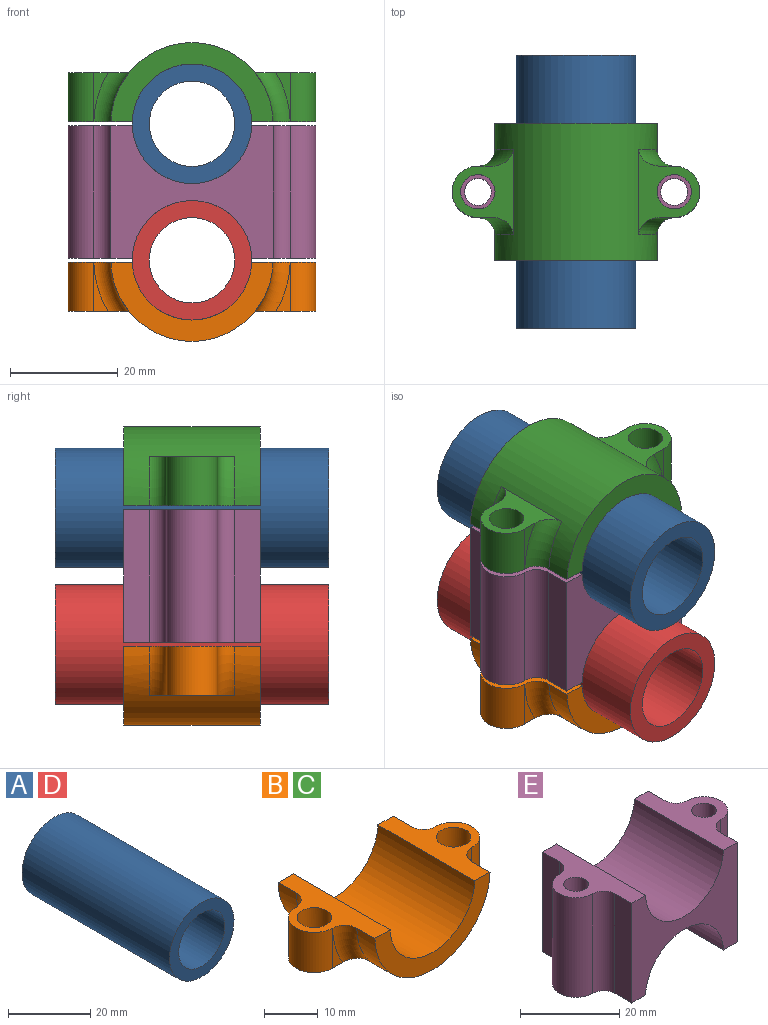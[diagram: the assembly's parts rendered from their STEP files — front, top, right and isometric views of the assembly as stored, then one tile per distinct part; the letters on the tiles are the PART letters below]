
ASSEMBLY  parts=5 mates=4
PART A: 4 faces, bbox 22.2x50.8x22.2 mm
  f0: cylinder r=7.94mm len=50.8mm, axis (0,1,0), area 2533.5mm2, adj f2,f3
  f1: cylinder r=11.11mm len=50.8mm, axis (0,1,0), area 3547mm2, adj f2,f3
  f2: plane 22.23x22.23mm, normal (0,-1,0), area 190mm2, adj f0,f1
  f3: plane 22.23x22.23mm, normal (0,1,0), area 190mm2, adj f0,f1
PART B: 20 faces, bbox 46.1x25.4x14.8 mm
  f0: cylinder r=15.09mm len=30.17mm, axis (0,1,0), area 868.6mm2, adj f1,f2,f4,f5,f6,f10,f11,f13
  f1: plane 25.43x11.96mm, normal (0,0,1), area 139.4mm2, adj f0,f3,f4,f5,f7,f8,f9,f10
  f2: plane 25.43x11.96mm, normal (0,0,1), area 139.4mm2, adj f0,f3,f4,f5,f14,f15,f16,f17
  f3: cylinder r=11.11mm len=25.4mm, axis (0,1,0), area 866.7mm2, adj f1,f2,f4,f5
  f4: plane 30.17x14.69mm, normal (0,-1,0), area 160.5mm2, adj f0,f1,f2,f3
  f5: plane 30.17x14.69mm, normal (0,1,0), area 160.5mm2, adj f0,f1,f2,f3
  f6: plane 15.9x11.34mm, normal (0,0,-1), area 71.7mm2, adj f0,f7,f8,f9,f10,f11,f12
  f7: plane 9.13x2.68mm, normal (0,-1,0), area 8.2mm2, adj f1,f6,f9,f11
  f8: plane 9.13x2.68mm, normal (0,1,0), area 8.2mm2, adj f1,f6,f9,f10
  f9: cylinder r=4.78mm len=9.55mm, axis (0,0,1), area 137mm2, adj f1,f6,f7,f8
  f10: torus R=18.26mm, axis (0,-1,0), area 48.9mm2, adj f0,f1,f6,f8
  f11: torus R=18.26mm, axis (0,-1,0), area 48.9mm2, adj f0,f1,f6,f7
  f12: cylinder r=3.2mm len=9.13mm, axis (0,0,-1), area 183.6mm2, adj f1,f6
  f13: plane 15.9x11.34mm, normal (0,0,-1), area 71.7mm2, adj f0,f14,f15,f16,f17,f18,f19
  f14: plane 9.13x2.68mm, normal (0,-1,0), area 8.2mm2, adj f2,f13,f16,f18
  f15: plane 9.13x2.68mm, normal (0,1,0), area 8.2mm2, adj f2,f13,f16,f17
  f16: cylinder r=4.78mm len=9.55mm, axis (0,0,-1), area 137mm2, adj f2,f13,f14,f15
  f17: torus R=18.26mm, axis (0,-1,0), area 48.9mm2, adj f0,f2,f13,f15
  f18: torus R=18.26mm, axis (0,-1,0), area 48.9mm2, adj f0,f2,f13,f14
  f19: cylinder r=3.2mm len=9.13mm, axis (0,0,-1), area 183.6mm2, adj f2,f13
PART C: same geometry as B
PART D: same geometry as A
PART E: 20 faces, bbox 46.1x25.4x24.6 mm
  f0: plane 24.61x4.75mm, normal (1,0,0), area 116.9mm2, adj f5,f8,f13,f19
  f1: plane 24.61x4.75mm, normal (-1,0,0), area 116.9mm2, adj f3,f8,f10,f17
  f2: plane 24.61x4.75mm, normal (-1,0,0), area 116.9mm2, adj f3,f7,f11,f17
  f3: plane 25.4x11.93mm, normal (0,0,-1), area 152mm2, adj f1,f2,f4,f7,f8,f9,f10,f11
  f4: cylinder r=11.11mm len=25.4mm, axis (0,1,0), area 866.7mm2, adj f3,f5,f7,f8
  f5: plane 25.4x11.93mm, normal (0,0,-1), area 152mm2, adj f0,f4,f6,f7,f8,f13,f14,f15
  f6: plane 24.61x4.75mm, normal (1,0,0), area 116.9mm2, adj f5,f7,f14,f19
  f7: plane 30.18x24.61mm, normal (0,-1,0), area 372.2mm2, adj f2,f3,f4,f5,f6,f17,f18,f19
  f8: plane 30.18x24.61mm, normal (0,1,0), area 372.2mm2, adj f0,f1,f3,f4,f5,f17,f18,f19
  f9: cylinder r=4.78mm len=24.61mm, axis (0,0,1), area 369.2mm2, adj f3,f10,f11,f17
  f10: cylinder r=3.17mm len=24.61mm, axis (0,0,1), area 122.7mm2, adj f1,f3,f9,f17
  f11: cylinder r=3.17mm len=24.61mm, axis (0,0,1), area 122.7mm2, adj f2,f3,f9,f17
  f12: cylinder r=2.5mm len=24.61mm, axis (0,0,1), area 386.6mm2, adj f3,f17
  f13: cylinder r=3.17mm len=24.61mm, axis (0,0,1), area 122.7mm2, adj f0,f5,f15,f19
  f14: cylinder r=3.17mm len=24.61mm, axis (0,0,1), area 122.7mm2, adj f5,f6,f15,f19
  f15: cylinder r=4.78mm len=24.61mm, axis (0,0,1), area 369.2mm2, adj f5,f13,f14,f19
  f16: cylinder r=2.5mm len=24.61mm, axis (0,0,1), area 386.6mm2, adj f5,f19
  f17: plane 25.4x11.93mm, normal (0,0,1), area 152mm2, adj f1,f2,f7,f8,f9,f10,f11,f12
  f18: cylinder r=11.11mm len=25.4mm, axis (0,1,0), area 866.7mm2, adj f7,f8,f17,f19
  f19: plane 25.4x11.93mm, normal (0,0,1), area 152mm2, adj f0,f6,f7,f8,f13,f14,f15,f16
PLACE A t=(0,0,25.4)mm
PLACE B t=(0,-25.4,0)mm
PLACE C rot(axis=(0,1,0),180deg) t=(0,-25.4,25.4)mm
PLACE D at identity fixed
PLACE E t=(0,-25.4,12.7)mm
MATE fastened D.f1 <-> E.f4  axis (0,1,0) through (0,-25.4,0)mm
MATE fastened C.f3 <-> A.f1  axis (0,1,0) through (0,-25.4,25.4)mm
MATE fastened A.f1 <-> E.f18  axis (0,1,0) through (0,-25.4,25.4)mm
MATE fastened B.f3 <-> D.f1  axis (0,1,0) through (0,-25.4,0)mm
